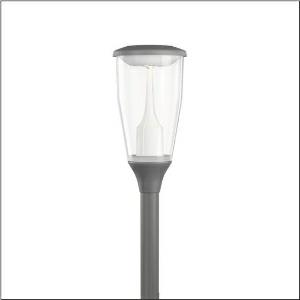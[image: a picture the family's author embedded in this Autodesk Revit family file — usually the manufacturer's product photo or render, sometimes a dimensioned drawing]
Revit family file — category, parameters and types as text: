
# Revit family: dl_11_iq___p1_0a_5xa5565ff14h000022_0ce9
name_source: partatom
category: Lighting Fixtures
units: mm (PartAtom-declared; Revit-internal decimal feet)

## family parameters
Cut with Voids When Loaded = No
Host = Face
Light Source = No
Part Type = Normal
Room Calculation Point = No
Round Connector Dimension = Use Diameter
Shared = No

## types (1)
- --- (1 x LED, 1530 lm, 10.5 W, 3000K)
    Apparent Load = 11 VA
    CIE Flux Codes = 34 63 91 95 100
    Color Rendering = 70
    Color Temperature = 3000K
    Default Elevation = 1800 mm
    Description = DL 11 iQ, mast luminaire, Module 540 iQ-SR, primary light control with 3 zone facetted reflector, of plastic, silver coated, highly specular, structured, primary optical cover: cover, of PMMA, transparent, light distribution: P1.0a, light emission: direct distribution, primary light characteristic: asymmetric, installation type: post-top, LED, High Power LED, rated luminous flux: 1.560lm, luminous efficacy: 149lm/W, light colour: 730, colour temperature: 3000K, control gear: iQ Street-Remote, control: Street-Remote, Auto-Match, Temp-Guard, Lumen-Switch, Night-Set, Smart-Wire, Light-Fading, Desk-Remote (wireless, voltage-free reading and setting of iQ features in the workshop via application-optimized NFC function/RFID function), optimised constant luminous flux control (CLO 2.0), mains connection: 220..240V, AC, 50/60Hz, connection cable pre-assembled, cable length: 5,5m, start of lifetime: 10W, end of service life: 11W, reduction: 5W, luminaire housing, upper part, of diecast aluminium, coated, Siteco® metallic grey (DB 702S), spigot size: 60mm (post-top), mounting height: 3..5m, post-top mast mounting element, of diecast aluminium, coated, Siteco® metallic grey (DB 702S), Module 540 iQ-SR, traffic white (RAL 9016), equipment: standard, protection rating (complete): IP66, insulation class (complete): insulation class II (safety insulation), certification: CE, ENEC, ENEC+, VDE, impact resistance: IK07, packaging unit: 1 piece

Light Distribution: P1.0a
    Height = 665 mm
    Lamp = 1 x LED
    Lamp Light Flux = 1530 lm
    Lamp Power = 10.5 W
    Lamp count = 1
    Length = 334 mm
    Luminous efficacy = 146 lm/W
    Manufacturer = Siteco
    ModVariant = No
    Model = 5XA5565FF14H000022
    Number of Poles = 1
    OnlyDefault = Yes
    Power Factor = 1
    Product Name = DL 11 iQ | P1.0a
    Product group = mast luminaire | pylon top
    ProductGroupID = 6100
    Protection Class = Protection class II
    Protection Degree = IP 66
    RLX_Detail_Level = 1
    RLX_Emergency_Light_Flux = 0 lm
    RLX_Emergency_Type = 0
    RLX_Emergency_Type_DB = No
    RlxData = <blob elided: 103413 chars, md5=648200b7>
    Socket = socket
    Standby Power = 0 W
    System Light Flux = 1530 lm
    System Power = 11 W
    Type Comments = factory setting: luminous flux: 100 % | dim-lin: 254 | 419 mA
    Type Image = l_1258354.jpg
    URL = http://relux.com
    VarID = @adj_113411
    Voltage = 0 V
    Weight = 0.00 kg
    Width = 0 mm  [stored 0 ft]

note: [stored X ft] marks values corroborated as IEEE doubles in the binary element streams (Revit-internal decimal feet)

## geometry (parser evidence)
native form markers: Blend x4, Sweep x9
no freeform markers — native parametric forms only
